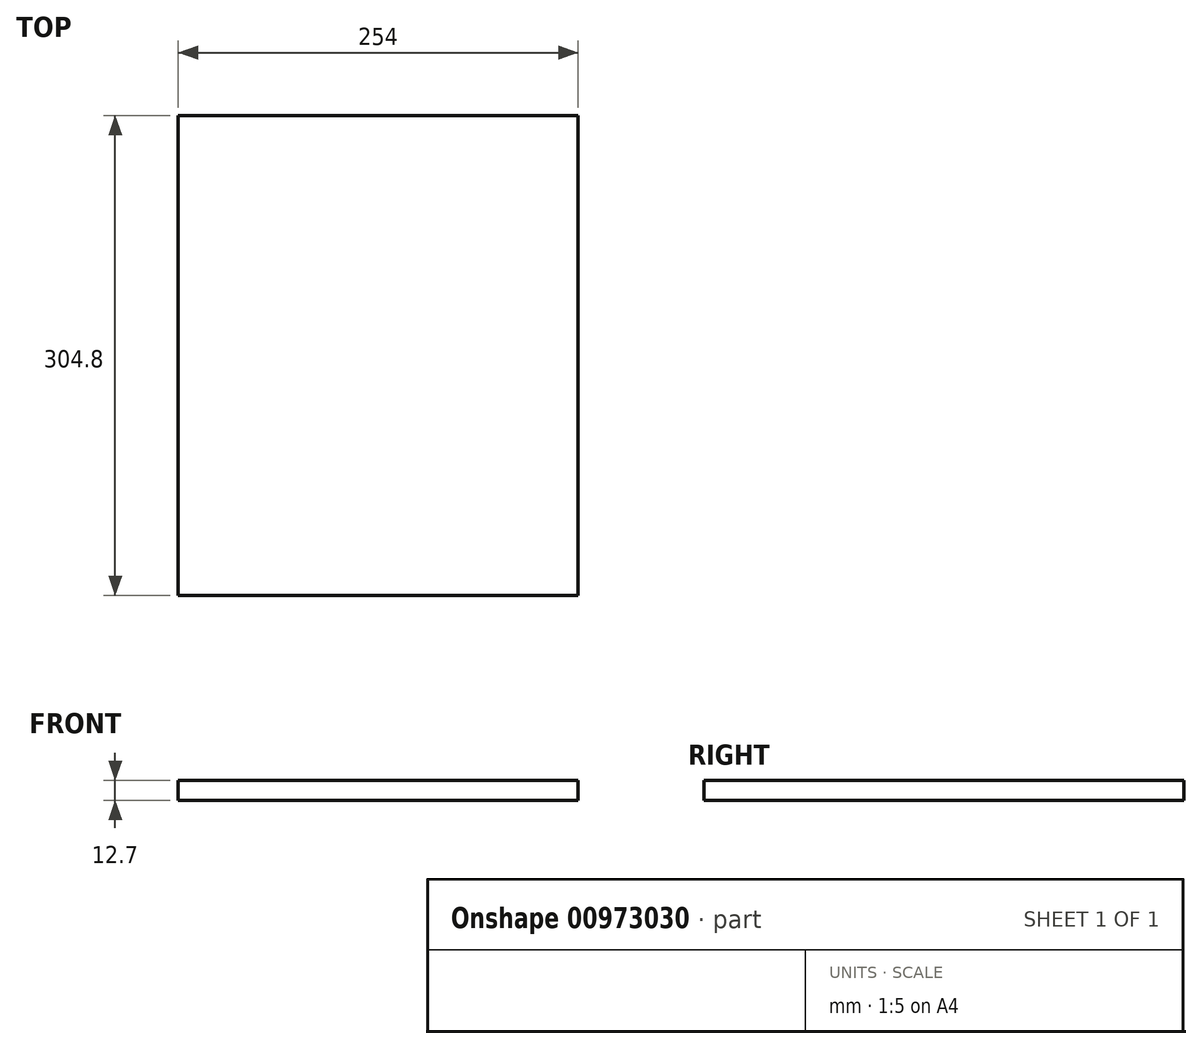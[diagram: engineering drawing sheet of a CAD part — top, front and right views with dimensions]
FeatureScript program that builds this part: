
annotation { "Feature Type Name" : "Feature", "Feature Type Description" : "" }
export const myFeature = defineFeature(function(context is Context, id is Id, definition is map)
    precondition{}
    {
        {
            var Q0;
            Q0=qCreatedBy(makeId("Top.planeOp"),FACE);
            var sketch = newSketch(context, id + "F0", { "sketchPlane" : qUnion([Q0])});
            skLineSegment(sketch, "E0.bottom", {"start": v(0, 0) * mm, "end": v(254, 0) * mm});
            skLineSegment(sketch, "E0.top", {"start": v(0, -304.8) * mm, "end": v(254, -304.8) * mm});
            skLineSegment(sketch, "E0.left", {"start": v(0, 0) * mm, "end": v(0, -304.8) * mm});
            skLineSegment(sketch, "E0.right", {"start": v(254, 0) * mm, "end": v(254, -304.8) * mm});
            skSolve(sketch);
        }
        {
            var Q0;
            Q0 = qSketchRegion(id + "F0", true);
            extrude(context, id + "F1", {"entities" : qUnion([Q0]), "depth" : 12.7 * mm, "offsetDistance" : 25.4 * mm});
        }
    });
